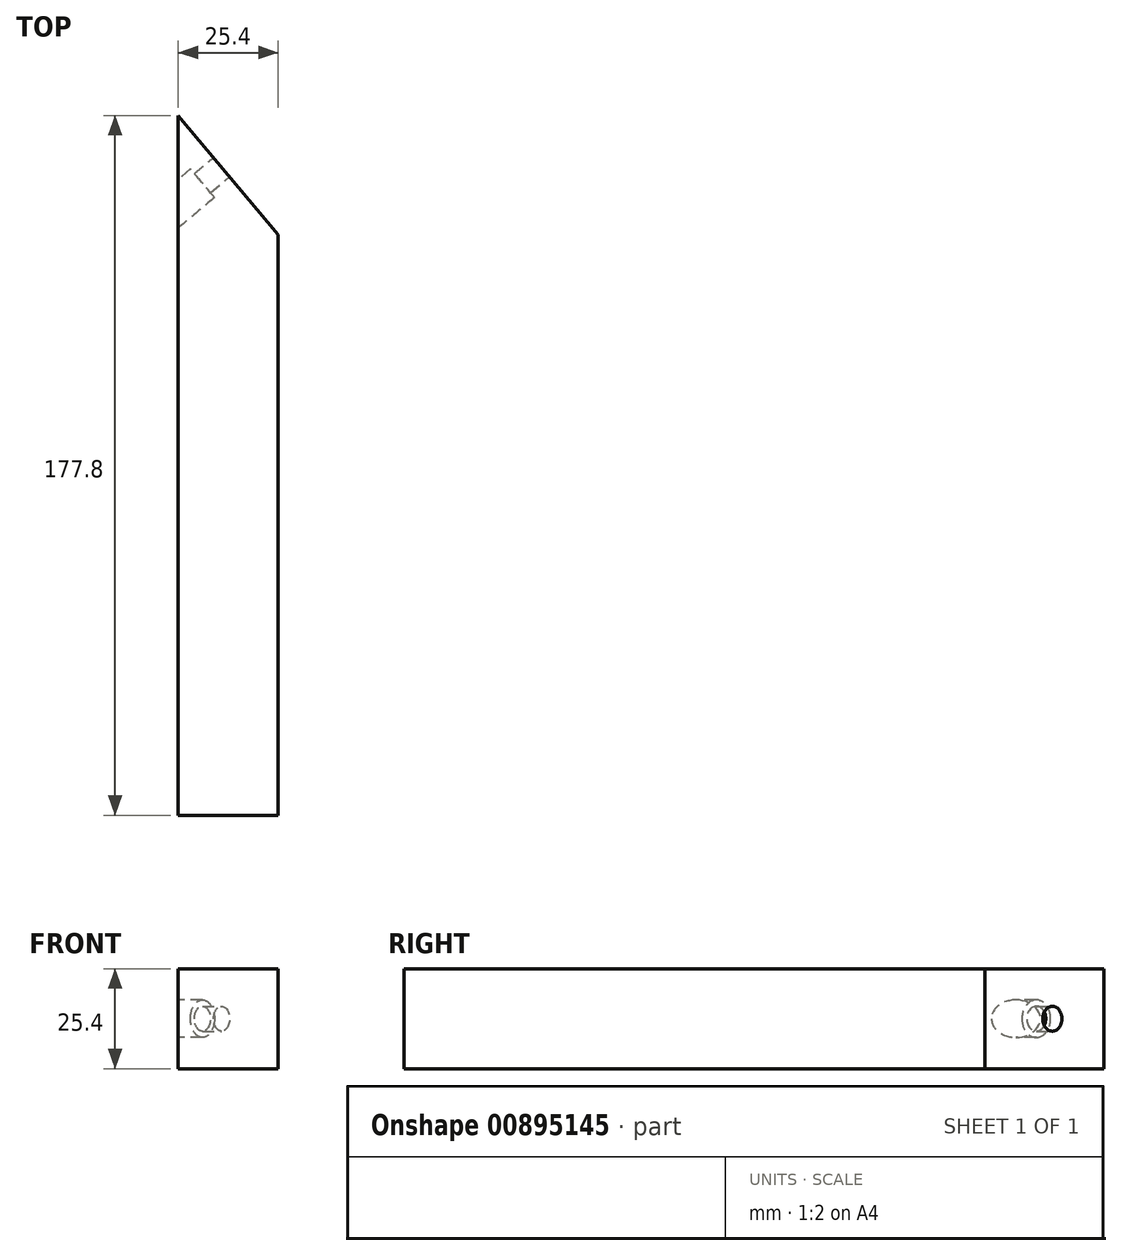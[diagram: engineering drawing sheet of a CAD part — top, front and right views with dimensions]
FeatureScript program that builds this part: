
annotation { "Feature Type Name" : "Feature", "Feature Type Description" : "" }
export const myFeature = defineFeature(function(context is Context, id is Id, definition is map)
    precondition{}
    {
        {
            var Q0;
            Q0=qCreatedBy(makeId("Front.planeOp"),FACE);
            var sketch = newSketch(context, id + "F0", { "sketchPlane" : qUnion([Q0])});
            skLineSegment(sketch, "E0.bottom", {"start": v(12.7, 12.7) * mm, "end": v(-12.7, 12.7) * mm});
            skLineSegment(sketch, "E0.top", {"start": v(12.7, -12.7) * mm, "end": v(-12.7, -12.7) * mm});
            skLineSegment(sketch, "E0.left", {"start": v(12.7, 12.7) * mm, "end": v(12.7, -12.7) * mm});
            skLineSegment(sketch, "E0.right", {"start": v(-12.7, 12.7) * mm, "end": v(-12.7, -12.7) * mm});
            skPoint(sketch, "E0.middle", {"position": v(0, 0) * mm});
            skLineSegment(sketch, "E1.bottom", {"start": v(-6.35, -12.7) * mm, "end": v(6.35, -12.7) * mm});
            skLineSegment(sketch, "E1.top", {"start": v(-6.35, 0) * mm, "end": v(6.35, 0) * mm});
            skLineSegment(sketch, "E1.left", {"start": v(-6.35, -12.7) * mm, "end": v(-6.35, 0) * mm});
            skLineSegment(sketch, "E1.right", {"start": v(6.35, -12.7) * mm, "end": v(6.35, 0) * mm});
            skSolve(sketch);
        }
        {
            var Q0;
            Q0=makeQuery(id+"F0.imprint","IMPRINT",FACE,{"disambiguationData":[TD([[makeQuery(id+"F0.imprint","IMPRINT",EDGE,{"derivedFrom":sQuery(id+"F0.wireOp",EDGE,"E0.bottom")}),1.0]])]});
            var Q1;
            Q1=makeQuery(id+"F0.imprint","IMPRINT",FACE,{"disambiguationData":[TD([[makeQuery(id+"F0.imprint","IMPRINT",EDGE,{"derivedFrom":sQuery(id+"F0.wireOp",EDGE,"E1.top")}),-1.0]])]});
            extrude(context, id + "F1", {"entities" : qUnion([Q0, Q1]), "depth" : 177.8 * mm, "offsetDistance" : 25.4 * mm});
        }
        {
            var Q0;
            Q0=makeQuery(id+"F1.opExtrude","SWEPT_FACE",FACE,{"disambiguationData":[OSD([sQuery(id+"F0.wireOp",EDGE,"E0.bottom")])]});
            var sketch = newSketch(context, id + "F2", { "sketchPlane" : qUnion([Q0])});
            skLineSegment(sketch, "E2", {"start": v(-12.7, 0) * mm, "end": v(12.7, -30.27) * mm});
            skLineSegment(sketch, "E3", {"start": v(12.7, -30.27) * mm, "end": v(12.7, 0) * mm});
            skLineSegment(sketch, "E4", {"start": v(12.7, 0) * mm, "end": v(-12.7, 0) * mm});
            skSolve(sketch);
        }
        {
            var Q0;
            Q0=makeQuery(id+"F2.imprint","IMPRINT",FACE,{"disambiguationData":[TD([[makeQuery(id+"F2.imprint","IMPRINT",EDGE,{"derivedFrom":sQuery(id+"F2.wireOp",EDGE,"E2")}),1.0]])]});
            extrude(context, id + "F3", {"entities" : qUnion([Q0]), "operationType" : NewBodyOperationType.REMOVE, "endBound" : BoundingType.THROUGH_ALL, "oppositeDirection" : true, "depth" : 25.4 * mm, "offsetDistance" : 25.4 * mm});
        }
        {
            var Q0;
            Q0=makeQuery(id+"F3.boolean.opBoolean","COPY",FACE,{"derivedFrom":makeQuery(id+"F3.opExtrude","SWEPT_FACE",FACE,{"disambiguationData":[OSD([sQuery(id+"F2.wireOp",EDGE,"E2")])]})});
            var sketch = newSketch(context, id + "F4", { "sketchPlane" : qUnion([Q0])});
            skCircle(sketch, "E5", {"center": v(-8.98, 0) * mm, "radius": 3.18 * mm});
            skSolve(sketch);
        }
        {
            var Q0;
            Q0 = qSketchRegion(id + "F4", true);
            extrude(context, id + "F5", {"entities" : qUnion([Q0]), "operationType" : NewBodyOperationType.REMOVE, "endBound" : BoundingType.THROUGH_ALL, "oppositeDirection" : true, "depth" : 25.4 * mm, "offsetDistance" : 25.4 * mm});
        }
        {
            var Q0;
            Q0=makeQuery(id+"F3.boolean.opBoolean","COPY",FACE,{"derivedFrom":makeQuery(id+"F3.opExtrude","SWEPT_FACE",FACE,{"disambiguationData":[OSD([sQuery(id+"F2.wireOp",EDGE,"E2")])]})});
            cPlane(context, id + "F6", {"entities" : qUnion([Q0]), "cplaneType" : CPlaneType.OFFSET, "offset" : 31.75 * mm, "oppositeDirection" : true, "width" : 152.4 * mm, "height" : 152.4 * mm});
        }
        {
            var Q0;
            Q0=qCreatedBy(id+"F6.planeOp",FACE);
            var sketch = newSketch(context, id + "F7", { "sketchPlane" : qUnion([Q0])});
            skCircle(sketch, "E6", {"center": v(-8.98, 0) * mm, "radius": 4.76 * mm});
            skCircle(sketch, "E7.0", {"center": v(-8.98, 0) * mm, "radius": 3.18 * mm});
            skSolve(sketch);
        }
        {
            var Q0;
            Q0 = qSketchRegion(id + "F7", true);
            var Q1;
            Q1=makeQuery(id+"F7.imprint","IMPRINT",FACE,{"disambiguationData":[TD([[makeQuery(id+"F7.imprint","IMPRINT",EDGE,{"derivedFrom":sQuery(id+"F7.wireOp",EDGE,"E7.0")}),1.0]])]});
            extrude(context, id + "F8", {"entities" : qUnion([Q0, Q1]), "operationType" : NewBodyOperationType.REMOVE, "depth" : 25.4 * mm, "offsetDistance" : 25.4 * mm});
        }
    });
